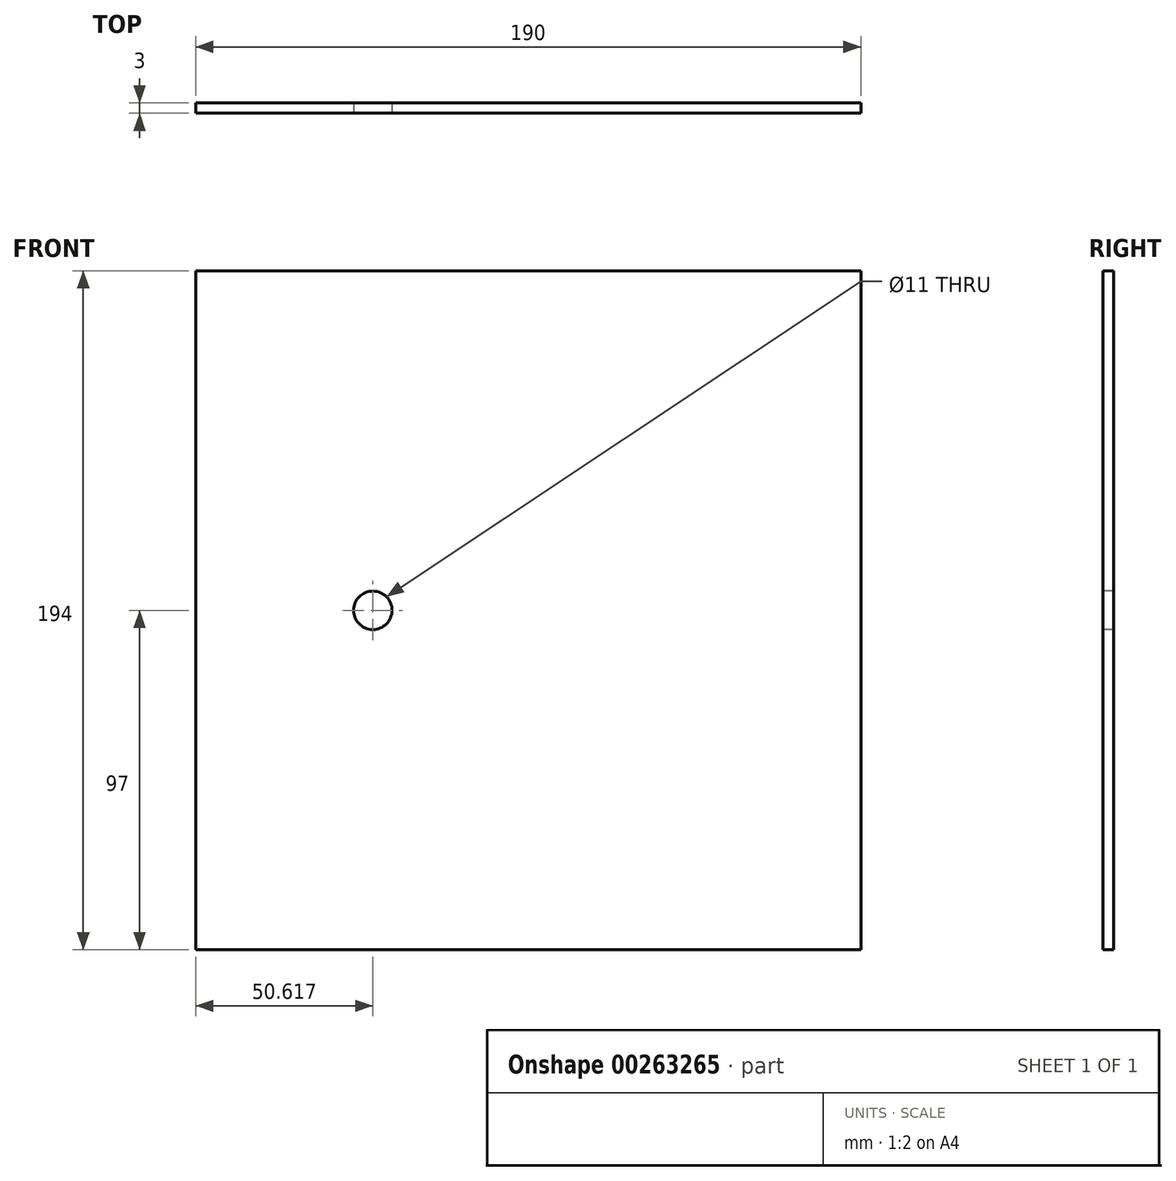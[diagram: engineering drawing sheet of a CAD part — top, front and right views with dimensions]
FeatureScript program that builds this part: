
annotation { "Feature Type Name" : "Feature", "Feature Type Description" : "" }
export const myFeature = defineFeature(function(context is Context, id is Id, definition is map)
    precondition{}
    {
        {
            var Q0;
            Q0=qCreatedBy(makeId("Front.planeOp"),FACE);
            var sketch = newSketch(context, id + "F0", { "sketchPlane" : qUnion([Q0])});
            skLineSegment(sketch, "E0.bottom", {"start": v(95, -97) * mm, "end": v(-95, -97) * mm});
            skLineSegment(sketch, "E0.top", {"start": v(95, 97) * mm, "end": v(-95, 97) * mm});
            skLineSegment(sketch, "E0.left", {"start": v(95, -97) * mm, "end": v(95, 97) * mm});
            skLineSegment(sketch, "E0.right", {"start": v(-95, -97) * mm, "end": v(-95, 97) * mm});
            skPoint(sketch, "E0.middle", {"position": v(0, 0) * mm});
            skSolve(sketch);
        }
        {
            var Q0;
            Q0 = qSketchRegion(id + "F0", true);
            extrude(context, id + "F1", {"entities" : qUnion([Q0]), "depth" : 3 * mm});
        }
        {
            var Q0;
            Q0=makeQuery(id+"F1.opExtrude","CAP_FACE",FACE,{"disambiguationData":[OSD([sQuery(id+"F0.wireOp",EDGE,"E0.bottom"),sQuery(id+"F0.wireOp",EDGE,"E0.top"),sQuery(id+"F0.wireOp",EDGE,"E0.left"),sQuery(id+"F0.wireOp",EDGE,"E0.right")])],"isStart":false});
            var sketch = newSketch(context, id + "F2", { "sketchPlane" : qUnion([Q0])});
            skLineSegment(sketch, "E1", {"start": v(-95, 0) * mm, "end": v(-44.38, 0) * mm});
            skLineSegment(sketch, "E2", {"start": v(-44.38, 0) * mm, "end": v(-68.56, -22.36) * mm});
            skLineSegment(sketch, "E3", {"start": v(-68.56, -22.36) * mm, "end": v(-95, 0) * mm});
            skSolve(sketch);
        }
        {
            var Q0;
            Q0=makeQuery(id+"F1.opExtrude","CAP_FACE",FACE,{"disambiguationData":[OSD([sQuery(id+"F0.wireOp",EDGE,"E0.bottom"),sQuery(id+"F0.wireOp",EDGE,"E0.top"),sQuery(id+"F0.wireOp",EDGE,"E0.left"),sQuery(id+"F0.wireOp",EDGE,"E0.right")])],"isStart":false});
            var sketch = newSketch(context, id + "F3", { "sketchPlane" : qUnion([Q0])});
            skCircle(sketch, "E4", {"center": v(-44.38, 0) * mm, "radius": 5.5 * mm});
            skSolve(sketch);
        }
        {
            var Q0;
            Q0 = qSketchRegion(id + "F3", true);
            extrude(context, id + "F4", {"entities" : qUnion([Q0]), "operationType" : NewBodyOperationType.REMOVE, "oppositeDirection" : true, "depth" : 30 * mm});
        }
    });
